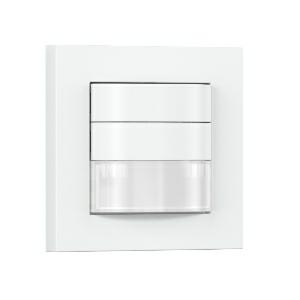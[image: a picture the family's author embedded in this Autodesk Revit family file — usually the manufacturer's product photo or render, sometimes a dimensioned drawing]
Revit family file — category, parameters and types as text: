
# Revit family: hf_180_032876
name_source: partatom
category: Elektroinstallationen
revit_build: Autodesk Revit 2016 (Build: 20190508_0715(x64)
units: mm (PartAtom-declared; Revit-internal decimal feet)

## family parameters
Basisbauteil = Fläche
Beim Laden mit Abzugskörper schneiden = Nein
Bemaßung runder Anschluss = Durchmesser verwenden
Beschriftungsausrichtung beibehalten = Nein
Gemeinsam genutzt = Nein
Raumberechnungspunkt = Nein
Teiletyp = Normal

## types (1)
- HF 180
    Apparent Load = 0 VA
    Beschreibung = Type: Presence detector; Dimensions (L x W x H): 21 x 80 x 80 mm; Power supply, detail: KNX bus; Sensor Technology: High frequency; Application, place: Indoors; Application, room: one-person office, corridor / aisle, function room / ancillary room, kitchenette, stairwell, WC / washroom, Indoors; Installation site: wall; Installation: Concealed wiring; HF-system: 5,8 GHz; Electronic scalability: Yes; Mechanical scalability: No; Mounting height: 1,20 – 2,2 m; Optimum mounting height: 1,2 m; Detection: also through glass, wood and stud walls; Detection angle: 180 °; Angle of aperture: 140 °; Sneak-by guard: Yes; Reach, radial: r = 8 m (101 m²); Reach, tangential: r = 8 m (101 m²); Twilight setting TEACH: Yes; Twilight setting: 2 – 1000 lx; Time setting: 60 sec – 255 min; Basic light level function: Yes; Basic light level function in per cent: 10 – 50 %; Basic light level function time: Permanently ON, 1-255 min, all night; Basic light level function percentage, from: 10 %; Basic light level function percentage, up to: 50 %; KNX functions: Light output 4x, Presence output, Light level, Constant-lighting control, Basic light level function, HVAC output, Integrated button, Temperature output, Humidity output; With bus coupling: No; Settings via: ETS software, Remote control, Bus, Smart Remote; IP-rating: IP20; Material: Plastic; Ambient temperature: 0 – 40 °C; Colour: white; Colour, RAL: 9010; Manufacturer's Warranty: 5 years; Version: KNX - white; PU1, EAN: 4007841032876
    Height = 80 mm  [stored 0.262467 ft]
    Hersteller = Steinel
    Length = 21 mm
    Maximum range = 7.902 m
    ModVariant = Nein
    Modell = 032876
    Mounting Type = Recessed
    Number of Poles = 1
    OnlyDefault = Ja
    Power Factor = 1
    Product Name = HF 180
    Product group = Sensor-switched indoor light
    ProductGroupID = 30
    Protection Class = Protection class II
    Protection Degree = IP 20
    RlxData = <blob elided: 124777 chars, md5=34fda900>
    Sensor characteristics = Sector <145°
    Sensor type = HF
    SensorDataFile = <blob elided: 8545 chars, md5=53bc5c10>
    Type of entry = Motion
    Typenbild = produkt1_032876.jpg
    Typenkommentare = Product without accessories
    URL = http://relux.com
    VarID = ---
    Voltage = 0 V
    Vorgabe-Ansicht = 1800 mm
    Weight = 0.00 kg
    Width = 80 mm  [stored 0.262467 ft]

note: [stored X ft] marks values corroborated as IEEE doubles in the binary element streams (Revit-internal decimal feet)

## geometry (parser evidence)
native form markers: Blend x4, Sweep x18
no freeform markers — native parametric forms only
